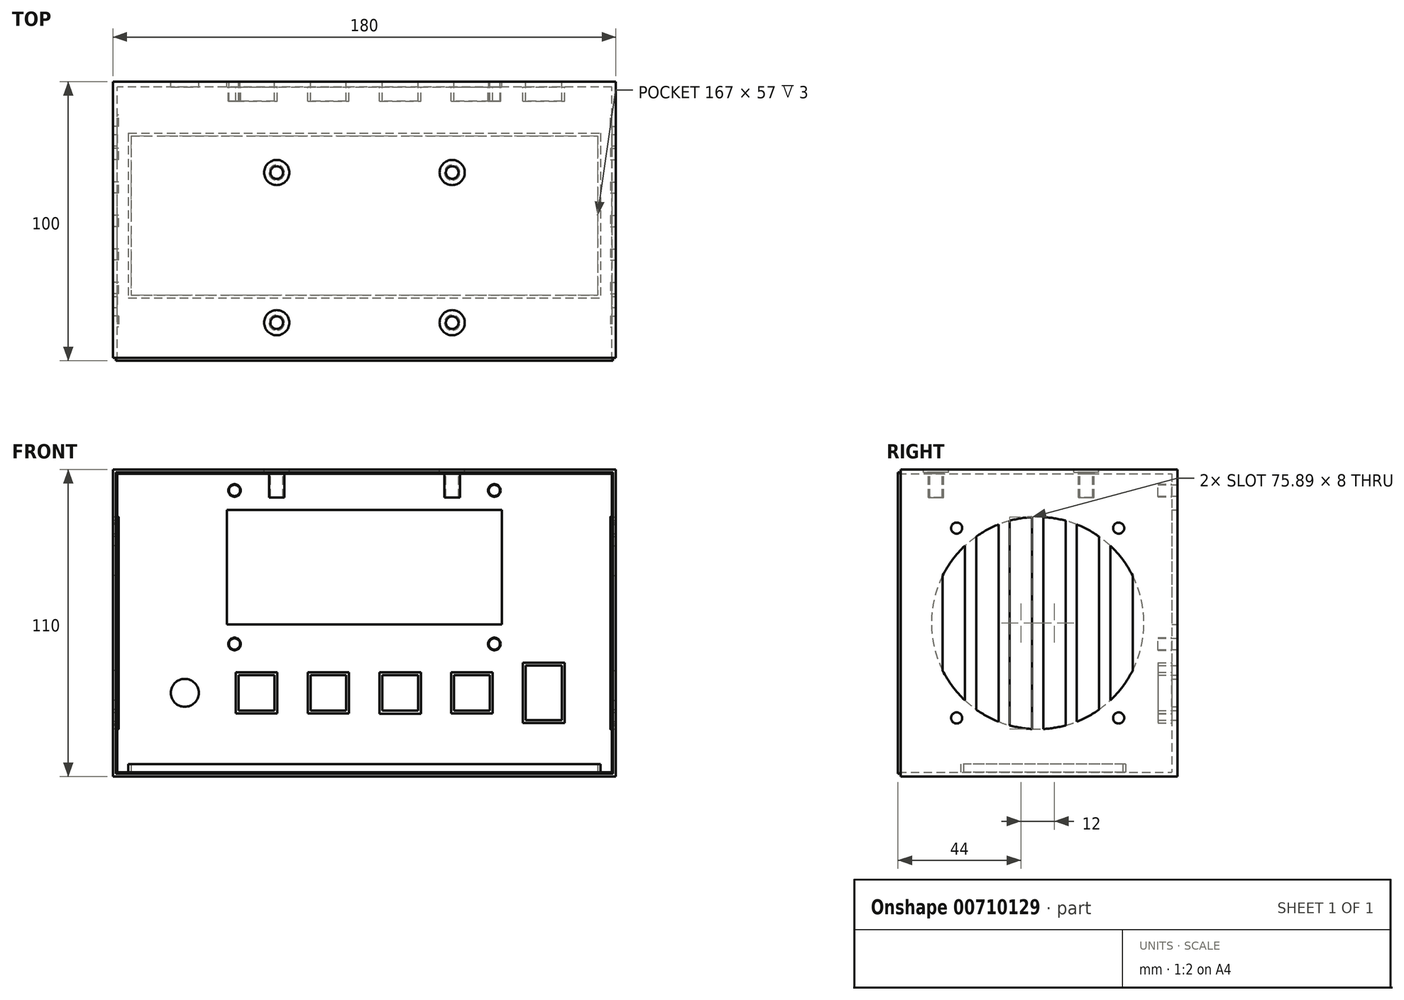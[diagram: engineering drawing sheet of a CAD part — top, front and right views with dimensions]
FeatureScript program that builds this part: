
annotation { "Feature Type Name" : "Feature", "Feature Type Description" : "" }
export const myFeature = defineFeature(function(context is Context, id is Id, definition is map)
    precondition{}
    {
        {
            var Q0;
            Q0=qCreatedBy(makeId("Front.planeOp"),FACE);
            var sketch = newSketch(context, id + "F0", { "sketchPlane" : qUnion([Q0])});
            skLineSegment(sketch, "E0.bottom", {"start": v(-90, 55) * mm, "end": v(90, 55) * mm});
            skLineSegment(sketch, "E0.top", {"start": v(-90, -55) * mm, "end": v(90, -55) * mm});
            skLineSegment(sketch, "E0.left", {"start": v(-90, 55) * mm, "end": v(-90, -55) * mm});
            skLineSegment(sketch, "E0.right", {"start": v(90, 55) * mm, "end": v(90, -55) * mm});
            skPoint(sketch, "E0.middle", {"position": v(0, 0) * mm});
            skPoint(sketch, "E1.middle", {"position": v(0, 20) * mm});
            skLineSegment(sketch, "E2.bottom", {"start": v(-49.25, 40.5) * mm, "end": v(49.25, 40.5) * mm});
            skLineSegment(sketch, "E2.top", {"start": v(-49.25, -0.5) * mm, "end": v(49.25, -0.5) * mm});
            skLineSegment(sketch, "E2.left", {"start": v(-49.25, 40.5) * mm, "end": v(-49.25, -0.5) * mm});
            skLineSegment(sketch, "E2.right", {"start": v(49.25, 40.5) * mm, "end": v(49.25, -0.5) * mm});
            skLineSegment(sketch, "E3", {"start": v(0, 20) * mm, "end": v(80.48, 20) * mm, "construction": true});
            skLineSegment(sketch, "E4", {"start": v(0, 20) * mm, "end": v(0, 44.12) * mm, "construction": true});
            skLineSegment(sketch, "E5", {"start": v(90, -25) * mm, "end": v(-90, -25) * mm, "construction": true});
            skPoint(sketch, "E6", {"position": v(46.5, 47.5) * mm});
            skPoint(sketch, "E7", {"position": v(46.5, -7.5) * mm});
            skPoint(sketch, "E8", {"position": v(-46.5, -7.5) * mm});
            skPoint(sketch, "E9", {"position": v(-46.5, 47.5) * mm});
            skPoint(sketch, "E10", {"position": v(-90, -25) * mm});
            skPoint(sketch, "E11.1.0.0", {"position": v(-64.3, -25) * mm});
            skPoint(sketch, "E11.2.0.0", {"position": v(-38.6, -25) * mm});
            skPoint(sketch, "E11.3.0.0", {"position": v(-12.9, -25) * mm});
            skPoint(sketch, "E11.4.0.0", {"position": v(12.8, -25) * mm});
            skPoint(sketch, "E11.5.0.0", {"position": v(38.5, -25) * mm});
            skPoint(sketch, "E11.6.0.0", {"position": v(64.2, -25) * mm});
            skLineSegment(sketch, "E11.direction1", {"start": v(-90, -25) * mm, "end": v(-64.3, -25) * mm, "construction": true});
            skLineSegment(sketch, "E12.bottom", {"start": v(70.7, -15.25) * mm, "end": v(57.7, -15.25) * mm});
            skLineSegment(sketch, "E12.top", {"start": v(70.7, -34.75) * mm, "end": v(57.7, -34.75) * mm});
            skLineSegment(sketch, "E12.left", {"start": v(70.7, -15.25) * mm, "end": v(70.7, -34.75) * mm});
            skLineSegment(sketch, "E12.right", {"start": v(57.7, -15.25) * mm, "end": v(57.7, -34.75) * mm});
            skLineSegment(sketch, "E13.bottom", {"start": v(44.9, -18.6) * mm, "end": v(32.1, -18.6) * mm});
            skLineSegment(sketch, "E13.top", {"start": v(44.9, -31.4) * mm, "end": v(32.1, -31.4) * mm});
            skLineSegment(sketch, "E13.left", {"start": v(44.9, -18.6) * mm, "end": v(44.9, -31.4) * mm});
            skLineSegment(sketch, "E13.right", {"start": v(32.1, -18.6) * mm, "end": v(32.1, -31.4) * mm});
            skLineSegment(sketch, "E14.bottom", {"start": v(19.2, -18.6) * mm, "end": v(6.4, -18.6) * mm});
            skLineSegment(sketch, "E14.top", {"start": v(19.2, -31.4) * mm, "end": v(6.4, -31.4) * mm});
            skLineSegment(sketch, "E14.left", {"start": v(19.2, -18.6) * mm, "end": v(19.2, -31.4) * mm});
            skLineSegment(sketch, "E14.right", {"start": v(6.4, -18.6) * mm, "end": v(6.4, -31.4) * mm});
            skLineSegment(sketch, "E15.bottom", {"start": v(-6.5, -18.6) * mm, "end": v(-19.3, -18.6) * mm});
            skLineSegment(sketch, "E15.top", {"start": v(-6.5, -31.4) * mm, "end": v(-19.3, -31.4) * mm});
            skLineSegment(sketch, "E15.left", {"start": v(-6.5, -18.6) * mm, "end": v(-6.5, -31.4) * mm});
            skLineSegment(sketch, "E15.right", {"start": v(-19.3, -18.6) * mm, "end": v(-19.3, -31.4) * mm});
            skLineSegment(sketch, "E16.bottom", {"start": v(-32.2, -18.6) * mm, "end": v(-45, -18.6) * mm});
            skLineSegment(sketch, "E16.top", {"start": v(-32.2, -31.4) * mm, "end": v(-45, -31.4) * mm});
            skLineSegment(sketch, "E16.left", {"start": v(-32.2, -18.6) * mm, "end": v(-32.2, -31.4) * mm});
            skLineSegment(sketch, "E16.right", {"start": v(-45, -18.6) * mm, "end": v(-45, -31.4) * mm});
            skCircle(sketch, "E17", {"center": v(-64.3, -25) * mm, "radius": 5 * mm});
            skSolve(sketch);
        }
        {
            var Q0;
            Q0=qCreatedBy(makeId("Front.planeOp"),FACE);
            var sketch = newSketch(context, id + "F1", { "sketchPlane" : qUnion([Q0])});
            skLineSegment(sketch, "E18.bottom", {"start": v(-90, 55) * mm, "end": v(90, 55) * mm});
            skLineSegment(sketch, "E18.top", {"start": v(-90, -55) * mm, "end": v(90, -55) * mm});
            skLineSegment(sketch, "E18.left", {"start": v(-90, 55) * mm, "end": v(-90, -55) * mm});
            skLineSegment(sketch, "E18.right", {"start": v(90, 55) * mm, "end": v(90, -55) * mm});
            skPoint(sketch, "E18.middle", {"position": v(0, 0) * mm});
            skLineSegment(sketch, "E19.bottom", {"start": v(88.5, 53.5) * mm, "end": v(-88.5, 53.5) * mm});
            skLineSegment(sketch, "E19.top", {"start": v(88.5, -53.5) * mm, "end": v(-88.5, -53.5) * mm});
            skLineSegment(sketch, "E19.left", {"start": v(88.5, 53.5) * mm, "end": v(88.5, -53.5) * mm});
            skLineSegment(sketch, "E19.right", {"start": v(-88.5, 53.5) * mm, "end": v(-88.5, -53.5) * mm});
            skSolve(sketch);
        }
        {
            var Q0;
            Q0=makeQuery(id+"F1.imprint","IMPRINT",FACE,{"disambiguationData":[TD([[makeQuery(id+"F1.imprint","IMPRINT",EDGE,{"derivedFrom":sQuery(id+"F1.wireOp",EDGE,"E18.bottom")}),-1.0]])]});
            extrude(context, id + "F2", {"entities" : qUnion([Q0]), "depth" : 100 * mm, "offsetDistance" : 25 * mm});
        }
        {
            var Q0;
            Q0=makeQuery(id+"F0.imprint","IMPRINT",FACE,{"disambiguationData":[TD([[makeQuery(id+"F0.imprint","IMPRINT",EDGE,{"derivedFrom":sQuery(id+"F0.wireOp",EDGE,"E0.bottom")}),-1.0]])]});
            extrude(context, id + "F3", {"entities" : qUnion([Q0]), "operationType" : NewBodyOperationType.ADD, "depth" : 2 * mm, "offsetDistance" : 25 * mm});
        }
        {
            var Q0;
            Q0=makeQuery(id+"F2.opExtrude","SWEPT_FACE",FACE,{"disambiguationData":[OSD([sQuery(id+"F1.wireOp",EDGE,"E18.right")])]});
            var sketch = newSketch(context, id + "F4", { "sketchPlane" : qUnion([Q0])});
            skCircle(sketch, "E20", {"center": v(-50, 0) * mm, "radius": 38 * mm});
            skCircle(sketch, "E21", {"center": v(-79, 34) * mm, "radius": 2 * mm});
            skCircle(sketch, "E22", {"center": v(-21, 34) * mm, "radius": 2 * mm});
            skCircle(sketch, "E23", {"center": v(-21, -34) * mm, "radius": 2 * mm});
            skCircle(sketch, "E24", {"center": v(-79, -34) * mm, "radius": 2 * mm});
            skSolve(sketch);
        }
        {
            var Q0;
            Q0=makeQuery(id+"F4.imprint","IMPRINT",FACE,{"disambiguationData":[TD([[makeQuery(id+"F4.imprint","IMPRINT",EDGE,{"derivedFrom":sQuery(id+"F4.wireOp",EDGE,"E20")}),1.0]])]});
            var Q1;
            Q1=makeQuery(id+"F4.imprint","IMPRINT",FACE,{"disambiguationData":[TD([[makeQuery(id+"F4.imprint","IMPRINT",EDGE,{"derivedFrom":sQuery(id+"F4.wireOp",EDGE,"E21")}),1.0]])]});
            var Q2;
            Q2=makeQuery(id+"F4.imprint","IMPRINT",FACE,{"disambiguationData":[TD([[makeQuery(id+"F4.imprint","IMPRINT",EDGE,{"derivedFrom":sQuery(id+"F4.wireOp",EDGE,"E22")}),1.0]])]});
            var Q3;
            Q3=makeQuery(id+"F4.imprint","IMPRINT",FACE,{"disambiguationData":[TD([[makeQuery(id+"F4.imprint","IMPRINT",EDGE,{"derivedFrom":sQuery(id+"F4.wireOp",EDGE,"E23")}),1.0]])]});
            var Q4;
            Q4=makeQuery(id+"F4.imprint","IMPRINT",FACE,{"disambiguationData":[TD([[makeQuery(id+"F4.imprint","IMPRINT",EDGE,{"derivedFrom":sQuery(id+"F4.wireOp",EDGE,"E24")}),1.0]])]});
            extrude(context, id + "F5", {"entities" : qUnion([Q0, Q1, Q2, Q3, Q4]), "operationType" : NewBodyOperationType.REMOVE, "endBound" : BoundingType.THROUGH_ALL, "oppositeDirection" : true, "depth" : 25 * mm, "offsetDistance" : 25 * mm});
        }
        {
            var Q0;
            Q0=makeQuery(id+"F2.opExtrude","CAP_FACE",FACE,{"disambiguationData":[OSD([sQuery(id+"F1.wireOp",EDGE,"E18.bottom"),sQuery(id+"F1.wireOp",EDGE,"E18.top"),sQuery(id+"F1.wireOp",EDGE,"E18.left"),sQuery(id+"F1.wireOp",EDGE,"E18.right"),sQuery(id+"F1.wireOp",EDGE,"E19.bottom"),sQuery(id+"F1.wireOp",EDGE,"E19.top"),sQuery(id+"F1.wireOp",EDGE,"E19.left"),sQuery(id+"F1.wireOp",EDGE,"E19.right")])],"isStart":false});
            var sketch = newSketch(context, id + "F6", { "sketchPlane" : qUnion([Q0])});
            skLineSegment(sketch, "E25.0", {"start": v(-89, 54) * mm, "end": v(-89, -54) * mm});
            skLineSegment(sketch, "E25.1", {"start": v(-89, 54) * mm, "end": v(89, 54) * mm});
            skLineSegment(sketch, "E25.2", {"start": v(89, 54) * mm, "end": v(89, -54) * mm});
            skLineSegment(sketch, "E25.3", {"start": v(-89, -54) * mm, "end": v(89, -54) * mm});
            skPoint(sketch, "E26.middle", {"position": v(0, 0) * mm});
            skLineSegment(sketch, "E27.bottom", {"start": v(90, -55) * mm, "end": v(-90, -55) * mm});
            skLineSegment(sketch, "E27.top", {"start": v(90, 55) * mm, "end": v(-90, 55) * mm});
            skLineSegment(sketch, "E27.left", {"start": v(90, -55) * mm, "end": v(90, 55) * mm});
            skLineSegment(sketch, "E27.right", {"start": v(-90, -55) * mm, "end": v(-90, 55) * mm});
            skSolve(sketch);
        }
        {
            var Q0;
            Q0=makeQuery(id+"F6.imprint","IMPRINT",FACE,{"disambiguationData":[TD([[makeQuery(id+"F6.imprint","IMPRINT",EDGE,{"derivedFrom":sQuery(id+"F6.wireOp",EDGE,"E25.0")}),-1.0]])]});
            extrude(context, id + "F7", {"entities" : qUnion([Q0]), "operationType" : NewBodyOperationType.REMOVE, "oppositeDirection" : true, "depth" : 1 * mm, "offsetDistance" : 25 * mm});
        }
        {
            var Q0;
            Q0=makeQuery(id+"FheHl0ono8cMDW9_1.boolean.opBoolean","MERGE",FACE,{"derivedFrom":[makeQuery(id+"F2.opExtrude","SWEPT_FACE",FACE,{"disambiguationData":[OSD([sQuery(id+"F1.wireOp",EDGE,"E18.left")])]}),makeQuery(id+"FheHl0ono8cMDW9_1.opExtrude","CAP_FACE",FACE,{"disambiguationData":[OSD([sQuery(id+"FRfqc8C0rzUA8EQ_1.wireOp",EDGE,"3ddf2b88-bfad-427e-ab28-662f7765b976"),sQuery(id+"FRfqc8C0rzUA8EQ_1.wireOp",EDGE,"5aca57dd-a018-4e32-b224-849ed8db4e17"),sQuery(id+"FRfqc8C0rzUA8EQ_1.wireOp",EDGE,"1ce7224f-1591-473c-b5f9-c58c96c1ab12"),sQuery(id+"FRfqc8C0rzUA8EQ_1.wireOp",EDGE,"42506cff-9ec2-4ce2-bbcb-edb3e44c1074"),sQuery(id+"FRfqc8C0rzUA8EQ_1.wireOp",EDGE,"e922a044-a7da-47d4-b1ae-a5b1ba72320e"),sQuery(id+"FRfqc8C0rzUA8EQ_1.wireOp",EDGE,"ad9f5a7e-a71e-4529-8620-4cbb4e42c406"),sQuery(id+"FRfqc8C0rzUA8EQ_1.wireOp",EDGE,"8e6d14b7-21ab-4ae3-99a2-d7d654472322"),sQuery(id+"FRfqc8C0rzUA8EQ_1.wireOp",EDGE,"9c565d4a-f9b7-468b-89ff-b5ffa7773f2e"),sQuery(id+"FRfqc8C0rzUA8EQ_1.wireOp",EDGE,"10bc4dd6-0511-492a-be69-319aa7d10057"),sQuery(id+"FRfqc8C0rzUA8EQ_1.wireOp",EDGE,"16b37615-f32d-474c-87a8-62d60c9ff4d5"),sQuery(id+"FRfqc8C0rzUA8EQ_1.wireOp",EDGE,"3e81fc04-e96b-4c8e-b3f0-e090be423896"),sQuery(id+"FRfqc8C0rzUA8EQ_1.wireOp",EDGE,"6c5e9223-72e3-416b-807a-06894ca1a87e"),sQuery(id+"FRfqc8C0rzUA8EQ_1.wireOp",EDGE,"1a4ea183-87b6-401a-bfbe-9de469da11c2")])],"isStart":false})]});
            var sketch = newSketch(context, id + "F8", { "sketchPlane" : qUnion([Q0])});
            skLineSegment(sketch, "E28", {"start": v(0, -55) * mm, "end": v(0, 55) * mm});
            skLineSegment(sketch, "E29", {"start": v(4, -55) * mm, "end": v(4, 55) * mm});
            skLineSegment(sketch, "E30.1.0.1", {"start": v(16, -16.97) * mm, "end": v(16, 16.97) * mm});
            skLineSegment(sketch, "E30.2.0.0", {"start": v(24, -27.71) * mm, "end": v(24, 27.71) * mm});
            skLineSegment(sketch, "E30.2.0.1", {"start": v(28, -30.98) * mm, "end": v(28, 30.98) * mm});
            skLineSegment(sketch, "E30.3.0.0", {"start": v(36, -35.33) * mm, "end": v(36, 35.33) * mm});
            skLineSegment(sketch, "E30.3.0.1", {"start": v(40, -36.66) * mm, "end": v(40, 36.66) * mm});
            skLineSegment(sketch, "E30.4.0.0", {"start": v(48, -37.95) * mm, "end": v(48, 37.95) * mm});
            skLineSegment(sketch, "E30.4.0.1", {"start": v(52, -37.95) * mm, "end": v(52, 37.95) * mm});
            skLineSegment(sketch, "E30.5.0.0", {"start": v(60, -36.66) * mm, "end": v(60, 36.66) * mm});
            skLineSegment(sketch, "E30.5.0.1", {"start": v(64, -35.33) * mm, "end": v(64, 35.33) * mm});
            skLineSegment(sketch, "E30.6.0.0", {"start": v(72, -30.98) * mm, "end": v(72, 30.98) * mm});
            skLineSegment(sketch, "E30.6.0.1", {"start": v(76, -27.71) * mm, "end": v(76, 27.71) * mm});
            skLineSegment(sketch, "E30.7.0.0", {"start": v(84, -16.97) * mm, "end": v(84, 16.97) * mm});
            skLineSegment(sketch, "E30.9.0.0", {"start": v(108, -55) * mm, "end": v(108, 55) * mm});
            skLineSegment(sketch, "E30.9.0.1", {"start": v(112, -55) * mm, "end": v(112, 55) * mm});
            skLineSegment(sketch, "E30.direction1", {"start": v(0, -55) * mm, "end": v(12, -55) * mm, "construction": true});
            skCircle(sketch, "E31", {"center": v(50, 0) * mm, "radius": 38 * mm});
            skPoint(sketch, "E31.first.point", {"position": v(17.35, -19.44) * mm});
            skPoint(sketch, "E31.second.point", {"position": v(69.63, -32.54) * mm});
            skPoint(sketch, "E31.third.point", {"position": v(64.71, 35.04) * mm});
            skPoint(sketch, "E32.orphan", {"position": v(28, -55) * mm});
            skPoint(sketch, "E33.orphan", {"position": v(24, -55) * mm});
            skPoint(sketch, "E34.orphan", {"position": v(36, -55) * mm});
            skPoint(sketch, "E35.orphan", {"position": v(40, -55) * mm});
            skPoint(sketch, "E36.orphan", {"position": v(48, -55) * mm});
            skPoint(sketch, "E37.orphan", {"position": v(52, -55) * mm});
            skPoint(sketch, "E38.orphan", {"position": v(60, -55) * mm});
            skPoint(sketch, "E39.orphan", {"position": v(64, -55) * mm});
            skPoint(sketch, "E40.orphan", {"position": v(72, -55) * mm});
            skPoint(sketch, "E41.orphan", {"position": v(76, -55) * mm});
            skPoint(sketch, "E42.orphan", {"position": v(84, -55) * mm});
            skPoint(sketch, "E43.orphan", {"position": v(88, -55) * mm});
            skPoint(sketch, "E44.orphan", {"position": v(16, -55) * mm});
            skPoint(sketch, "E45.orphan", {"position": v(16, 55) * mm});
            skPoint(sketch, "E46.orphan", {"position": v(24, 55) * mm});
            skPoint(sketch, "E47.orphan", {"position": v(28, 55) * mm});
            skPoint(sketch, "E48.orphan", {"position": v(36, 55) * mm});
            skPoint(sketch, "E49.orphan", {"position": v(40, 55) * mm});
            skPoint(sketch, "E50.orphan", {"position": v(48, 55) * mm});
            skPoint(sketch, "E51.orphan", {"position": v(52, 55) * mm});
            skPoint(sketch, "E52.orphan", {"position": v(60, 55) * mm});
            skPoint(sketch, "E53.orphan", {"position": v(64, 55) * mm});
            skPoint(sketch, "E54.orphan", {"position": v(72, 55) * mm});
            skPoint(sketch, "E55.orphan", {"position": v(76, 55) * mm});
            skPoint(sketch, "E56.orphan", {"position": v(84, 55) * mm});
            skSolve(sketch);
        }
        {
            var Q0;
            {var subQ0=sQuery(id+"F8.wireOp",EDGE,"E30.2.0.0");Q0=makeQuery(id+"F8.imprint","IMPRINT",FACE,{"disambiguationData":[TD([[makeQuery(id+"F8.imprint","IMPRINT",EDGE,{"derivedFrom":subQ0}),-1.0]])]});}
            var Q1;
            {var subQ0=sQuery(id+"F8.wireOp",EDGE,"E30.1.0.1");Q1=makeQuery(id+"F8.imprint","IMPRINT",FACE,{"disambiguationData":[TD([[makeQuery(id+"F8.imprint","IMPRINT",EDGE,{"derivedFrom":subQ0}),1.0]])]});}
            var Q2;
            {var subQ0=sQuery(id+"F8.wireOp",EDGE,"E30.3.0.0");Q2=makeQuery(id+"F8.imprint","IMPRINT",FACE,{"disambiguationData":[TD([[makeQuery(id+"F8.imprint","IMPRINT",EDGE,{"derivedFrom":subQ0}),-1.0]])]});}
            var Q3;
            {var subQ0=sQuery(id+"F8.wireOp",EDGE,"E30.4.0.0");Q3=makeQuery(id+"F8.imprint","IMPRINT",FACE,{"disambiguationData":[TD([[makeQuery(id+"F8.imprint","IMPRINT",EDGE,{"derivedFrom":subQ0}),-1.0]])]});}
            var Q4;
            {var subQ0=sQuery(id+"F8.wireOp",EDGE,"E30.5.0.0");Q4=makeQuery(id+"F8.imprint","IMPRINT",FACE,{"disambiguationData":[TD([[makeQuery(id+"F8.imprint","IMPRINT",EDGE,{"derivedFrom":subQ0}),-1.0]])]});}
            var Q5;
            {var subQ0=sQuery(id+"F8.wireOp",EDGE,"E30.6.0.0");Q5=makeQuery(id+"F8.imprint","IMPRINT",FACE,{"disambiguationData":[TD([[makeQuery(id+"F8.imprint","IMPRINT",EDGE,{"derivedFrom":subQ0}),-1.0]])]});}
            var Q6;
            {var subQ0=sQuery(id+"F8.wireOp",EDGE,"E30.7.0.0");Q6=makeQuery(id+"F8.imprint","IMPRINT",FACE,{"disambiguationData":[TD([[makeQuery(id+"F8.imprint","IMPRINT",EDGE,{"derivedFrom":subQ0}),-1.0]])]});}
            extrude(context, id + "F9", {"entities" : qUnion([Q0, Q1, Q2, Q3, Q4, Q5, Q6]), "operationType" : NewBodyOperationType.ADD, "oppositeDirection" : true, "depth" : 2 * mm, "offsetDistance" : 25 * mm});
        }
        {
            var Q0;
            Q0=makeQuery(id+"FheHl0ono8cMDW9_1.boolean.opBoolean","MERGE",FACE,{"derivedFrom":[makeQuery(id+"F2.opExtrude","SWEPT_FACE",FACE,{"disambiguationData":[OSD([sQuery(id+"F1.wireOp",EDGE,"E18.right")])]}),makeQuery(id+"FheHl0ono8cMDW9_1.opExtrude","CAP_FACE",FACE,{"disambiguationData":[OSD([sQuery(id+"FRfqc8C0rzUA8EQ_1.wireOp",EDGE,"3ddf2b88-bfad-427e-ab28-662f7765b976"),sQuery(id+"FRfqc8C0rzUA8EQ_1.wireOp",EDGE,"5aca57dd-a018-4e32-b224-849ed8db4e17"),sQuery(id+"FRfqc8C0rzUA8EQ_1.wireOp",EDGE,"1ce7224f-1591-473c-b5f9-c58c96c1ab12"),sQuery(id+"FRfqc8C0rzUA8EQ_1.wireOp",EDGE,"42506cff-9ec2-4ce2-bbcb-edb3e44c1074"),sQuery(id+"FRfqc8C0rzUA8EQ_1.wireOp",EDGE,"e922a044-a7da-47d4-b1ae-a5b1ba72320e"),sQuery(id+"FRfqc8C0rzUA8EQ_1.wireOp",EDGE,"ad9f5a7e-a71e-4529-8620-4cbb4e42c406"),sQuery(id+"FRfqc8C0rzUA8EQ_1.wireOp",EDGE,"8e6d14b7-21ab-4ae3-99a2-d7d654472322"),sQuery(id+"FRfqc8C0rzUA8EQ_1.wireOp",EDGE,"9c565d4a-f9b7-468b-89ff-b5ffa7773f2e"),sQuery(id+"FRfqc8C0rzUA8EQ_1.wireOp",EDGE,"10bc4dd6-0511-492a-be69-319aa7d10057"),sQuery(id+"FRfqc8C0rzUA8EQ_1.wireOp",EDGE,"16b37615-f32d-474c-87a8-62d60c9ff4d5"),sQuery(id+"FRfqc8C0rzUA8EQ_1.wireOp",EDGE,"3e81fc04-e96b-4c8e-b3f0-e090be423896"),sQuery(id+"FRfqc8C0rzUA8EQ_1.wireOp",EDGE,"6c5e9223-72e3-416b-807a-06894ca1a87e"),sQuery(id+"FRfqc8C0rzUA8EQ_1.wireOp",EDGE,"1a4ea183-87b6-401a-bfbe-9de469da11c2")])],"isStart":true})]});
            var sketch = newSketch(context, id + "F10", { "sketchPlane" : qUnion([Q0])});
            skLineSegment(sketch, "E57", {"start": v(0, 55) * mm, "end": v(0, -55) * mm});
            skLineSegment(sketch, "E58", {"start": v(-4, 55) * mm, "end": v(-4, -55) * mm});
            skLineSegment(sketch, "E59.1.0.1", {"start": v(-16, 16.97) * mm, "end": v(-16, -16.97) * mm});
            skLineSegment(sketch, "E59.2.0.0", {"start": v(-24, 27.71) * mm, "end": v(-24, -27.71) * mm});
            skLineSegment(sketch, "E59.2.0.1", {"start": v(-28, 30.98) * mm, "end": v(-28, -30.98) * mm});
            skLineSegment(sketch, "E59.3.0.0", {"start": v(-36, 35.33) * mm, "end": v(-36, -35.33) * mm});
            skLineSegment(sketch, "E59.3.0.1", {"start": v(-40, 36.66) * mm, "end": v(-40, -36.66) * mm});
            skLineSegment(sketch, "E59.4.0.0", {"start": v(-48, 37.95) * mm, "end": v(-48, -37.95) * mm});
            skLineSegment(sketch, "E59.4.0.1", {"start": v(-52, 37.95) * mm, "end": v(-52, -37.95) * mm});
            skLineSegment(sketch, "E59.5.0.0", {"start": v(-60, 36.66) * mm, "end": v(-60, -36.66) * mm});
            skLineSegment(sketch, "E59.5.0.1", {"start": v(-64, 35.33) * mm, "end": v(-64, -35.33) * mm});
            skLineSegment(sketch, "E59.6.0.0", {"start": v(-72, 30.98) * mm, "end": v(-72, -30.98) * mm});
            skLineSegment(sketch, "E59.6.0.1", {"start": v(-76, 27.71) * mm, "end": v(-76, -27.71) * mm});
            skLineSegment(sketch, "E59.7.0.0", {"start": v(-84, 16.97) * mm, "end": v(-84, -16.97) * mm});
            skLineSegment(sketch, "E59.9.0.0", {"start": v(-108, 55) * mm, "end": v(-108, -55) * mm});
            skLineSegment(sketch, "E59.9.0.1", {"start": v(-112, 55) * mm, "end": v(-112, -55) * mm});
            skLineSegment(sketch, "E59.direction1", {"start": v(0, 55) * mm, "end": v(-12, 55) * mm, "construction": true});
            skCircle(sketch, "E60", {"center": v(-50, 0) * mm, "radius": 38 * mm});
            skPoint(sketch, "E60.first.point", {"position": v(-19.76, 23) * mm});
            skPoint(sketch, "E60.second.point", {"position": v(-67.37, 33.8) * mm});
            skPoint(sketch, "E60.third.point", {"position": v(-66.48, -34.24) * mm});
            skPoint(sketch, "E61.orphan", {"position": v(-28, 60) * mm});
            skPoint(sketch, "E62.orphan", {"position": v(-24, 60) * mm});
            skPoint(sketch, "E63.orphan", {"position": v(-36, 60) * mm});
            skPoint(sketch, "E64.orphan", {"position": v(-40, 60) * mm});
            skPoint(sketch, "E65.orphan", {"position": v(-48, 60) * mm});
            skPoint(sketch, "E66.orphan", {"position": v(-52, 60) * mm});
            skPoint(sketch, "E67.orphan", {"position": v(-60, 60) * mm});
            skPoint(sketch, "E68.orphan", {"position": v(-64, 60) * mm});
            skPoint(sketch, "E69.orphan", {"position": v(-72, 60) * mm});
            skPoint(sketch, "E70.orphan", {"position": v(-76, 60) * mm});
            skPoint(sketch, "E71.orphan", {"position": v(-84, 60) * mm});
            skPoint(sketch, "E72.orphan", {"position": v(-88, 55) * mm});
            skPoint(sketch, "E73.orphan", {"position": v(-16, 60) * mm});
            skPoint(sketch, "E74.orphan", {"position": v(-16, -50) * mm});
            skPoint(sketch, "E75.orphan", {"position": v(-24, -50) * mm});
            skPoint(sketch, "E76.orphan", {"position": v(-28, -50) * mm});
            skPoint(sketch, "E77.orphan", {"position": v(-36, -50) * mm});
            skPoint(sketch, "E78.orphan", {"position": v(-40, -50) * mm});
            skPoint(sketch, "E79.orphan", {"position": v(-48, -50) * mm});
            skPoint(sketch, "E80.orphan", {"position": v(-52, -50) * mm});
            skPoint(sketch, "E81.orphan", {"position": v(-60, -50) * mm});
            skPoint(sketch, "E82.orphan", {"position": v(-64, -50) * mm});
            skPoint(sketch, "E83.orphan", {"position": v(-72, -50) * mm});
            skPoint(sketch, "E84.orphan", {"position": v(-76, -50) * mm});
            skPoint(sketch, "E85.orphan", {"position": v(-84, -50) * mm});
            skPoint(sketch, "E86.first.point", {"position": v(-67.9, 33.52) * mm});
            skPoint(sketch, "E86.second.point", {"position": v(-35.98, 35.32) * mm});
            skPoint(sketch, "E86.third.point", {"position": v(-35.98, 35.32) * mm});
            skSolve(sketch);
        }
        {
            var Q0;
            {var subQ0=sQuery(id+"F10.wireOp",EDGE,"E59.1.0.1");Q0=makeQuery(id+"F10.imprint","IMPRINT",FACE,{"disambiguationData":[TD([[makeQuery(id+"F10.imprint","IMPRINT",EDGE,{"derivedFrom":subQ0}),1.0]])]});}
            var Q1;
            {var subQ0=sQuery(id+"F10.wireOp",EDGE,"E59.2.0.0");Q1=makeQuery(id+"F10.imprint","IMPRINT",FACE,{"disambiguationData":[TD([[makeQuery(id+"F10.imprint","IMPRINT",EDGE,{"derivedFrom":subQ0}),-1.0]])]});}
            var Q2;
            {var subQ0=sQuery(id+"F10.wireOp",EDGE,"E59.3.0.0");Q2=makeQuery(id+"F10.imprint","IMPRINT",FACE,{"disambiguationData":[TD([[makeQuery(id+"F10.imprint","IMPRINT",EDGE,{"derivedFrom":subQ0}),-1.0]])]});}
            var Q3;
            {var subQ0=sQuery(id+"F10.wireOp",EDGE,"E59.4.0.0");Q3=makeQuery(id+"F10.imprint","IMPRINT",FACE,{"disambiguationData":[TD([[makeQuery(id+"F10.imprint","IMPRINT",EDGE,{"derivedFrom":subQ0}),-1.0]])]});}
            var Q4;
            {var subQ0=sQuery(id+"F10.wireOp",EDGE,"E59.5.0.0");Q4=makeQuery(id+"F10.imprint","IMPRINT",FACE,{"disambiguationData":[TD([[makeQuery(id+"F10.imprint","IMPRINT",EDGE,{"derivedFrom":subQ0}),-1.0]])]});}
            var Q5;
            {var subQ0=sQuery(id+"F10.wireOp",EDGE,"E59.6.0.0");Q5=makeQuery(id+"F10.imprint","IMPRINT",FACE,{"disambiguationData":[TD([[makeQuery(id+"F10.imprint","IMPRINT",EDGE,{"derivedFrom":subQ0}),-1.0]])]});}
            var Q6;
            {var subQ0=sQuery(id+"F10.wireOp",EDGE,"E59.7.0.0");Q6=makeQuery(id+"F10.imprint","IMPRINT",FACE,{"disambiguationData":[TD([[makeQuery(id+"F10.imprint","IMPRINT",EDGE,{"derivedFrom":subQ0}),-1.0]])]});}
            extrude(context, id + "F11", {"entities" : qUnion([Q0, Q1, Q2, Q3, Q4, Q5, Q6]), "operationType" : NewBodyOperationType.ADD, "oppositeDirection" : true, "depth" : 2 * mm, "offsetDistance" : 25 * mm});
        }
        {
            var Q0;
            Q0=sQuery(id+"F0.wireOp",VERTEX,"E6");
            var Q1;
            Q1=sQuery(id+"F0.wireOp",VERTEX,"E7");
            var Q2;
            Q2=sQuery(id+"F0.wireOp",VERTEX,"E8");
            var Q3;
            Q3=sQuery(id+"F0.wireOp",VERTEX,"E9");
            var Q4;
            Q4=makeQuery(id+"F2.opExtrude","SWEPT_BODY",BODY,{"disambiguationData":[OSD([sQuery(id+"F1.wireOp",EDGE,"E18.bottom"),sQuery(id+"F1.wireOp",EDGE,"E18.top"),sQuery(id+"F1.wireOp",EDGE,"E18.left"),sQuery(id+"F1.wireOp",EDGE,"E18.right"),sQuery(id+"F1.wireOp",EDGE,"E19.bottom"),sQuery(id+"F1.wireOp",EDGE,"E19.top"),sQuery(id+"F1.wireOp",EDGE,"E19.left"),sQuery(id+"F1.wireOp",EDGE,"E19.right")])]});
            hole(context, id + "F12", {"style" : HoleStyle.C_BORE, "endStyle" : HoleEndStyle.BLIND, "oppositeDirection" : true, "holeDiameter" : 4 * mm, "cBoreDiameter" : 4 * mm, "cBoreDepth" : 0 * mm, "majorDiameter" : 5 * mm, "holeDepth" : 3 * mm, "isTappedThrough" : true, "tappedDepth" : 12 * mm, "tapClearance" : 3, "locations" : qUnion([Q0, Q1, Q2, Q3]), "scope" : qUnion([Q4])});
        }
        {
            var Q0;
            Q0=makeQuery(id+"F2.opExtrude","SWEPT_FACE",FACE,{"disambiguationData":[OSD([sQuery(id+"F1.wireOp",EDGE,"E18.bottom")])]});
            var sketch = newSketch(context, id + "F13", { "sketchPlane" : qUnion([Q0])});
            skLineSegment(sketch, "E87.bottom", {"start": v(35, -90) * mm, "end": v(-35, -90) * mm, "construction": true});
            skLineSegment(sketch, "E87.top", {"start": v(35, -29) * mm, "end": v(-35, -29) * mm, "construction": true});
            skLineSegment(sketch, "E87.left", {"start": v(35, -90) * mm, "end": v(35, -29) * mm, "construction": true});
            skLineSegment(sketch, "E87.right", {"start": v(-35, -90) * mm, "end": v(-35, -29) * mm, "construction": true});
            skPoint(sketch, "E87.middle", {"position": v(0, -59.5) * mm});
            skCircle(sketch, "E88", {"center": v(31.4, -86.4) * mm, "radius": 2.25 * mm});
            skCircle(sketch, "E89", {"center": v(-31.4, -86.4) * mm, "radius": 2.25 * mm});
            skCircle(sketch, "E90", {"center": v(-31.4, -32.6) * mm, "radius": 2.25 * mm});
            skCircle(sketch, "E91", {"center": v(31.4, -32.6) * mm, "radius": 2.25 * mm});
            skPoint(sketch, "E92", {"position": v(0, 0) * mm});
            skPoint(sketch, "E93.positionSnap0", {"position": v(-35, -59.5) * mm});
            skPoint(sketch, "E94", {"position": v(-90, -49.5) * mm});
            skPoint(sketch, "E95", {"position": v(-90, -59.5) * mm});
            skCircle(sketch, "E96", {"center": v(-31.4, -32.6) * mm, "radius": 2.75 * mm});
            skCircle(sketch, "E97", {"center": v(-31.4, -86.4) * mm, "radius": 2.75 * mm});
            skCircle(sketch, "E98", {"center": v(31.4, -86.4) * mm, "radius": 2.75 * mm});
            skCircle(sketch, "E99", {"center": v(31.4, -32.6) * mm, "radius": 2.75 * mm});
            skSolve(sketch);
        }
        {
            var Q0;
            Q0 = qSketchRegion(id + "F13", true);
            extrude(context, id + "F14", {"entities" : qUnion([Q0]), "operationType" : NewBodyOperationType.ADD, "oppositeDirection" : true, "depth" : 10 * mm, "offsetDistance" : 25 * mm});
        }
        {
            var Q0;
            Q0=sQuery(id+"F13.wireOp",VERTEX,"E90.center");
            var Q1;
            Q1=sQuery(id+"F13.wireOp",VERTEX,"E91.center");
            var Q2;
            Q2=sQuery(id+"F13.wireOp",VERTEX,"E88.center");
            var Q3;
            Q3=sQuery(id+"F13.wireOp",VERTEX,"E89.center");
            var Q4;
            Q4=makeQuery(id+"F2.opExtrude","SWEPT_BODY",BODY,{"disambiguationData":[OSD([sQuery(id+"F1.wireOp",EDGE,"E18.bottom"),sQuery(id+"F1.wireOp",EDGE,"E18.top"),sQuery(id+"F1.wireOp",EDGE,"E18.left"),sQuery(id+"F1.wireOp",EDGE,"E18.right"),sQuery(id+"F1.wireOp",EDGE,"E19.bottom"),sQuery(id+"F1.wireOp",EDGE,"E19.top"),sQuery(id+"F1.wireOp",EDGE,"E19.left"),sQuery(id+"F1.wireOp",EDGE,"E19.right")])]});
            hole(context, id + "F15", {"style" : HoleStyle.C_BORE, "endStyle" : HoleEndStyle.BLIND, "holeDiameter" : 4.5 * mm, "cBoreDiameter" : 9 * mm, "cBoreDepth" : 1 * mm, "majorDiameter" : 5 * mm, "holeDepth" : 10 * mm, "isTappedThrough" : true, "tappedDepth" : 12 * mm, "tapClearance" : 3, "locations" : qUnion([Q0, Q1, Q2, Q3]), "scope" : qUnion([Q4])});
        }
        {
            var Q0;
            {var subQ0=sQuery(id+"F0.wireOp",EDGE,"E2.right");var subQ1=sQuery(id+"F0.wireOp",EDGE,"E2.left");var subQ2=sQuery(id+"F0.wireOp",EDGE,"E2.top");var subQ3=sQuery(id+"F0.wireOp",EDGE,"E2.bottom");Q0=makeQuery(id+"F17.boolean.opBoolean","SPLIT",FACE,{"disambiguationData":[TD([makeQuery(id+"F2.opExtrude","SWEPT_FACE",FACE,{"disambiguationData":[OSD([sQuery(id+"F1.wireOp",EDGE,"E19.bottom")])]})])],"derivedFrom":makeQuery(id+"F3.opExtrude","CAP_FACE",FACE,{"disambiguationData":[OSD([sQuery(id+"F0.wireOp",EDGE,"E0.bottom"),sQuery(id+"F0.wireOp",EDGE,"E0.top"),sQuery(id+"F0.wireOp",EDGE,"E0.left"),sQuery(id+"F0.wireOp",EDGE,"E0.right"),subQ3,subQ2,subQ1,subQ0])],"isStart":false})});}
            var sketch = newSketch(context, id + "F16", { "sketchPlane" : qUnion([Q0])});
            skPoint(sketch, "E100", {"position": v(-46.5, -7.5) * mm});
            skPoint(sketch, "E101", {"position": v(46.5, -7.5) * mm});
            skPoint(sketch, "E102", {"position": v(46.5, 47.5) * mm});
            skPoint(sketch, "E103", {"position": v(-46.5, 47.5) * mm});
            skCircle(sketch, "E104", {"center": v(-46.5, -7.5) * mm, "radius": 2.25 * mm});
            skCircle(sketch, "E105", {"center": v(-46.5, -7.5) * mm, "radius": 2 * mm});
            skCircle(sketch, "E106", {"center": v(46.5, -7.5) * mm, "radius": 2.25 * mm});
            skCircle(sketch, "E107", {"center": v(46.5, -7.5) * mm, "radius": 2 * mm});
            skCircle(sketch, "E108", {"center": v(46.5, 47.5) * mm, "radius": 2.25 * mm});
            skCircle(sketch, "E109", {"center": v(46.5, 47.5) * mm, "radius": 2 * mm});
            skCircle(sketch, "E110", {"center": v(-46.5, 47.5) * mm, "radius": 2.25 * mm});
            skCircle(sketch, "E111", {"center": v(-46.5, 47.5) * mm, "radius": 2 * mm});
            skLineSegment(sketch, "E112.bottom", {"start": v(-45, -18.6) * mm, "end": v(-32.2, -18.6) * mm});
            skLineSegment(sketch, "E112.top", {"start": v(-45, -31.4) * mm, "end": v(-32.2, -31.4) * mm});
            skLineSegment(sketch, "E112.left", {"start": v(-45, -18.6) * mm, "end": v(-45, -31.4) * mm});
            skLineSegment(sketch, "E112.right", {"start": v(-32.2, -18.6) * mm, "end": v(-32.2, -31.4) * mm});
            skLineSegment(sketch, "E113.bottom", {"start": v(-19.3, -18.6) * mm, "end": v(-6.5, -18.6) * mm});
            skLineSegment(sketch, "E113.top", {"start": v(-19.3, -31.4) * mm, "end": v(-6.5, -31.4) * mm});
            skLineSegment(sketch, "E113.left", {"start": v(-19.3, -18.6) * mm, "end": v(-19.3, -31.4) * mm});
            skLineSegment(sketch, "E113.right", {"start": v(-6.5, -18.6) * mm, "end": v(-6.5, -31.4) * mm});
            skLineSegment(sketch, "E114.bottom", {"start": v(6.4, -18.6) * mm, "end": v(19.2, -18.6) * mm});
            skLineSegment(sketch, "E114.top", {"start": v(6.4, -31.4) * mm, "end": v(19.2, -31.4) * mm});
            skLineSegment(sketch, "E114.left", {"start": v(6.4, -18.6) * mm, "end": v(6.4, -31.4) * mm});
            skLineSegment(sketch, "E114.right", {"start": v(19.2, -18.6) * mm, "end": v(19.2, -31.4) * mm});
            skLineSegment(sketch, "E115.bottom", {"start": v(32.1, -18.6) * mm, "end": v(44.9, -18.6) * mm});
            skLineSegment(sketch, "E115.top", {"start": v(32.1, -31.4) * mm, "end": v(44.9, -31.4) * mm});
            skLineSegment(sketch, "E115.left", {"start": v(32.1, -18.6) * mm, "end": v(32.1, -31.4) * mm});
            skLineSegment(sketch, "E115.right", {"start": v(44.9, -18.6) * mm, "end": v(44.9, -31.4) * mm});
            skLineSegment(sketch, "E116.bottom", {"start": v(57.7, -15.25) * mm, "end": v(70.7, -15.25) * mm});
            skLineSegment(sketch, "E116.top", {"start": v(57.7, -34.75) * mm, "end": v(70.7, -34.75) * mm});
            skLineSegment(sketch, "E116.left", {"start": v(57.7, -15.25) * mm, "end": v(57.7, -34.75) * mm});
            skLineSegment(sketch, "E116.right", {"start": v(70.7, -15.25) * mm, "end": v(70.7, -34.75) * mm});
            skLineSegment(sketch, "E117.bottom", {"start": v(-46, -17.6) * mm, "end": v(-31.2, -17.6) * mm});
            skLineSegment(sketch, "E117.top", {"start": v(-46, -32.4) * mm, "end": v(-31.2, -32.4) * mm});
            skLineSegment(sketch, "E117.left", {"start": v(-46, -17.6) * mm, "end": v(-46, -32.4) * mm});
            skLineSegment(sketch, "E117.right", {"start": v(-31.2, -17.6) * mm, "end": v(-31.2, -32.4) * mm});
            skLineSegment(sketch, "E118.bottom", {"start": v(-20.3, -17.6) * mm, "end": v(-5.5, -17.6) * mm});
            skLineSegment(sketch, "E118.top", {"start": v(-20.3, -32.4) * mm, "end": v(-5.5, -32.4) * mm});
            skLineSegment(sketch, "E118.left", {"start": v(-20.3, -17.6) * mm, "end": v(-20.3, -32.4) * mm});
            skLineSegment(sketch, "E118.right", {"start": v(-5.5, -17.6) * mm, "end": v(-5.5, -32.4) * mm});
            skLineSegment(sketch, "E119.bottom", {"start": v(5.4, -17.6) * mm, "end": v(20.2, -17.6) * mm});
            skLineSegment(sketch, "E119.top", {"start": v(5.4, -32.47) * mm, "end": v(20.2, -32.47) * mm});
            skLineSegment(sketch, "E119.left", {"start": v(5.4, -17.6) * mm, "end": v(5.4, -32.47) * mm});
            skLineSegment(sketch, "E119.right", {"start": v(20.2, -17.6) * mm, "end": v(20.2, -32.47) * mm});
            skLineSegment(sketch, "E120.bottom", {"start": v(31.1, -17.6) * mm, "end": v(45.9, -17.6) * mm});
            skLineSegment(sketch, "E120.top", {"start": v(31.1, -32.4) * mm, "end": v(45.9, -32.4) * mm});
            skLineSegment(sketch, "E120.left", {"start": v(31.1, -17.6) * mm, "end": v(31.1, -32.4) * mm});
            skLineSegment(sketch, "E120.right", {"start": v(45.9, -17.6) * mm, "end": v(45.9, -32.4) * mm});
            skLineSegment(sketch, "E121.bottom", {"start": v(56.7, -14.25) * mm, "end": v(71.7, -14.25) * mm});
            skLineSegment(sketch, "E121.top", {"start": v(56.7, -35.75) * mm, "end": v(71.7, -35.75) * mm});
            skLineSegment(sketch, "E121.left", {"start": v(56.7, -14.25) * mm, "end": v(56.7, -35.75) * mm});
            skLineSegment(sketch, "E121.right", {"start": v(71.7, -14.25) * mm, "end": v(71.7, -35.75) * mm});
            skSolve(sketch);
        }
        {
            var Q0;
            Q0 = qSketchRegion(id + "F16", true);
            extrude(context, id + "F17", {"entities" : qUnion([Q0]), "operationType" : NewBodyOperationType.ADD, "depth" : 5 * mm, "offsetDistance" : 25 * mm});
        }
        {
            var Q0;
            Q0=makeQuery(id+"F2.opExtrude","SWEPT_FACE",FACE,{"disambiguationData":[OSD([sQuery(id+"F1.wireOp",EDGE,"E19.top")])]});
            var sketch = newSketch(context, id + "F18", { "sketchPlane" : qUnion([Q0])});
            skLineSegment(sketch, "E122.bottom", {"start": v(-83.5, -19.5) * mm, "end": v(83.5, -19.5) * mm});
            skLineSegment(sketch, "E122.top", {"start": v(-83.5, -76.5) * mm, "end": v(83.5, -76.5) * mm});
            skLineSegment(sketch, "E122.left", {"start": v(-83.5, -19.5) * mm, "end": v(-83.5, -76.5) * mm});
            skLineSegment(sketch, "E122.right", {"start": v(83.5, -19.5) * mm, "end": v(83.5, -76.5) * mm});
            skPoint(sketch, "E122.middle", {"position": v(0, -48) * mm});
            skLineSegment(sketch, "E123.bottom", {"start": v(-84.5, -18.5) * mm, "end": v(84.5, -18.5) * mm});
            skLineSegment(sketch, "E123.top", {"start": v(-84.5, -77.5) * mm, "end": v(84.5, -77.5) * mm});
            skLineSegment(sketch, "E123.left", {"start": v(-84.5, -18.5) * mm, "end": v(-84.5, -77.5) * mm});
            skLineSegment(sketch, "E123.right", {"start": v(84.5, -18.5) * mm, "end": v(84.5, -77.5) * mm});
            skSolve(sketch);
        }
        {
            var Q0;
            Q0 = qSketchRegion(id + "F18", true);
            extrude(context, id + "F19", {"entities" : qUnion([Q0]), "operationType" : NewBodyOperationType.ADD, "depth" : 3 * mm, "offsetDistance" : 25 * mm});
        }
    });
